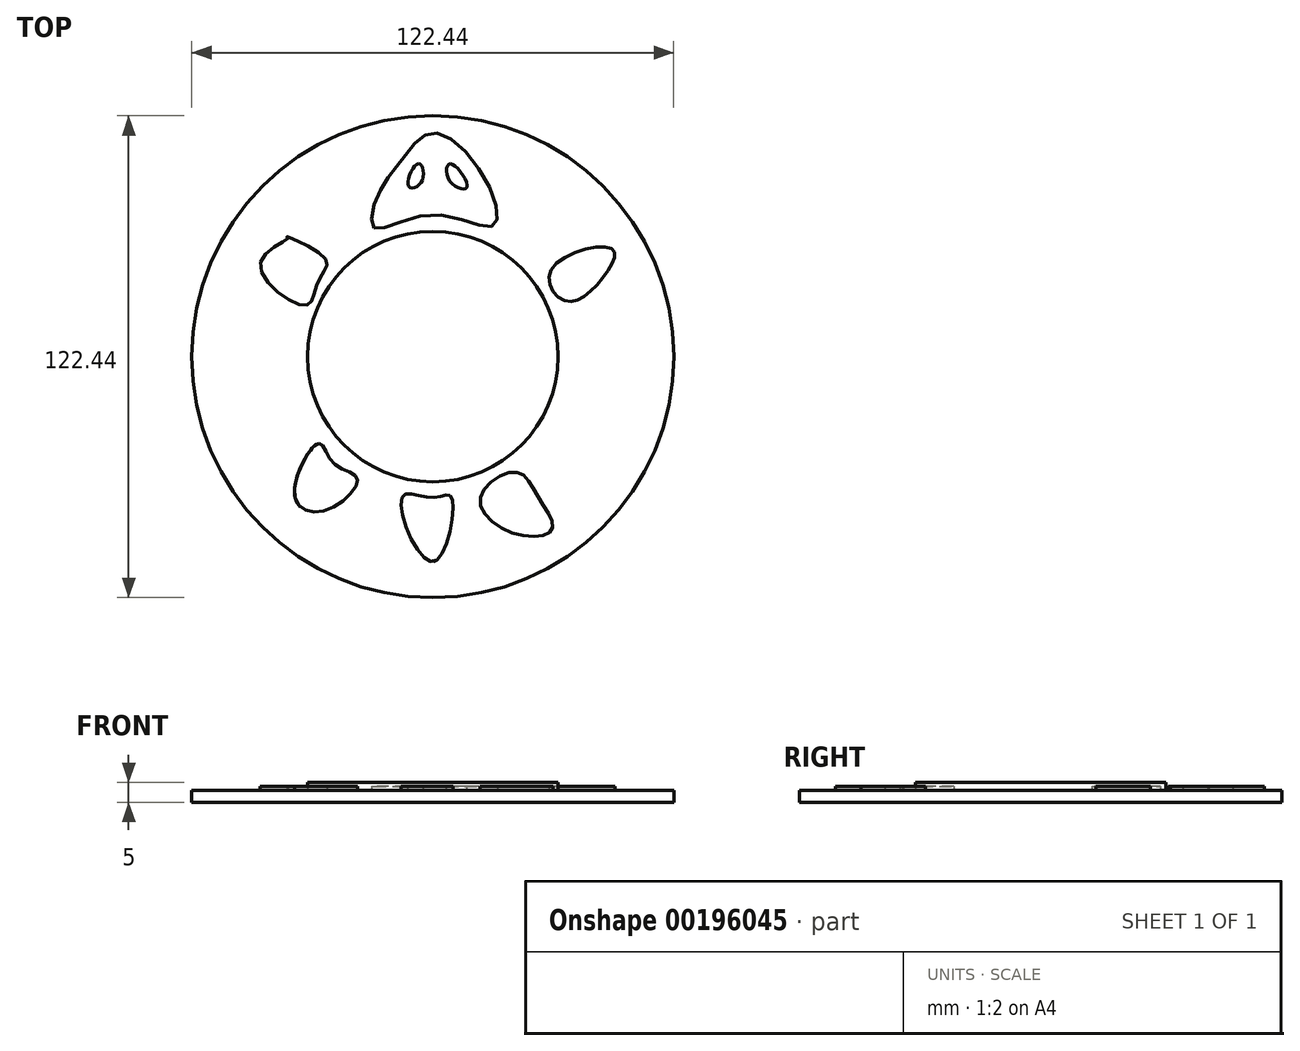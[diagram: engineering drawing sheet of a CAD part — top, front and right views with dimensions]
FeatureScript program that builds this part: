
annotation { "Feature Type Name" : "Feature", "Feature Type Description" : "" }
export const myFeature = defineFeature(function(context is Context, id is Id, definition is map)
    precondition{}
    {
        {
            var Q0;
            Q0=qCreatedBy(makeId("Top.planeOp"),FACE);
            var sketch = newSketch(context, id + "F0", { "sketchPlane" : qUnion([Q0])});
            skCircle(sketch, "E0", {"center": v(0, 0) * mm, "radius": 61.22 * mm});
            skSolve(sketch);
        }
        {
            var Q0;
            Q0 = qSketchRegion(id + "F0", true);
            extrude(context, id + "F1", {"entities" : qUnion([Q0]), "depth" : 3 * mm});
        }
        {
            var Q0;
            Q0=makeQuery(id+"F1.opExtrude","CAP_FACE",FACE,{"disambiguationData":[OSD([sQuery(id+"F0.wireOp",EDGE,"E0")])],"isStart":false});
            var sketch = newSketch(context, id + "F2", { "sketchPlane" : qUnion([Q0])});
            skCircle(sketch, "E1", {"center": v(0, 0) * mm, "radius": 31.81 * mm});
            skSolve(sketch);
        }
        {
            var Q0;
            Q0=makeQuery(id+"F2.imprint","IMPRINT",FACE,{"disambiguationData":[TD([[makeQuery(id+"F2.imprint","IMPRINT",EDGE,{"derivedFrom":sQuery(id+"F2.wireOp",EDGE,"E1")}),1.0]])]});
            extrude(context, id + "F3", {"entities" : qUnion([Q0]), "operationType" : NewBodyOperationType.ADD, "depth" : 2 * mm});
        }
        {
            var Q0;
            Q0=makeQuery(id+"F1.opExtrude","CAP_FACE",FACE,{"disambiguationData":[OSD([sQuery(id+"F0.wireOp",EDGE,"E0")])],"isStart":false});
            var sketch = newSketch(context, id + "F4", { "sketchPlane" : qUnion([Q0])});
            skFitSpline(sketch, "E2", {"points": [v(-14.88, 32.7) * mm, v(0, 36.08) * mm, v(15.44, 33.27) * mm, v(13.2, 45.34) * mm, v(0, 56.85) * mm, v(-7.3, 50.68) * mm, v(-13.76, 41.41) * mm, v(-14.88, 32.7) * mm]});
            skSolve(sketch);
        }
        {
            var Q0;
            Q0=makeQuery(id+"F4.imprint","IMPRINT",FACE,{"disambiguationData":[TD([[makeQuery(id+"F4.imprint","IMPRINT",EDGE,{"derivedFrom":sQuery(id+"F4.wireOp",EDGE,"E2")}),1.0]])]});
            extrude(context, id + "F5", {"entities" : qUnion([Q0]), "operationType" : NewBodyOperationType.ADD, "depth" : 1 * mm});
        }
        {
            var Q0;
            Q0=makeQuery(id+"F1.opExtrude","CAP_FACE",FACE,{"disambiguationData":[OSD([sQuery(id+"F0.wireOp",EDGE,"E0")])],"isStart":false});
            var sketch = newSketch(context, id + "F6", { "sketchPlane" : qUnion([Q0])});
            skFitSpline(sketch, "E3", {"points": [v(-27.23, 24.85) * mm, v(-37.06, 30.46) * mm, v(-36.78, 30.18) * mm, v(-43.8, 23.72) * mm, v(-32.29, 13.05) * mm, v(-29.2, 18.95) * mm, v(-27.23, 24.85) * mm]});
            skFitSpline(sketch, "E4", {"points": [v(-28.92, -22.04) * mm, v(-25.27, -27.1) * mm, v(-19.1, -31.02) * mm, v(-27.51, -39.16) * mm, v(-35.1, -35.23) * mm, v(-28.92, -22.04) * mm]});
            skFitSpline(sketch, "E5", {"points": [v(12.07, -35.8) * mm, v(21.06, -29.34) * mm, v(26.67, -35.51) * mm, v(30.32, -43.94) * mm, v(20.21, -44.78) * mm, v(12.07, -35.8) * mm]});
            skFitSpline(sketch, "E6", {"points": [v(30.04, 22.04) * mm, v(33.69, 14.18) * mm, v(43.24, 20.07) * mm, v(45.48, 27.37) * mm, v(30.04, 22.04) * mm]});
            skFitSpline(sketch, "E7", {"points": [v(-7.86, -35.8) * mm, v(0, -52.08) * mm, v(4.77, -35.8) * mm, v(0, -35.8) * mm, v(-7.86, -35.8) * mm]});
            skSolve(sketch);
        }
        {
            var Q0;
            Q0=makeQuery(id+"F6.imprint","IMPRINT",FACE,{"disambiguationData":[TD([[makeQuery(id+"F6.imprint","IMPRINT",EDGE,{"derivedFrom":sQuery(id+"F6.wireOp",EDGE,"E3")}),1.0]])]});
            var Q1;
            Q1=makeQuery(id+"F6.imprint","IMPRINT",FACE,{"disambiguationData":[TD([[makeQuery(id+"F6.imprint","IMPRINT",EDGE,{"derivedFrom":sQuery(id+"F6.wireOp",EDGE,"E4")}),-1.0]])]});
            var Q2;
            Q2=makeQuery(id+"F6.imprint","IMPRINT",FACE,{"disambiguationData":[TD([[makeQuery(id+"F6.imprint","IMPRINT",EDGE,{"derivedFrom":sQuery(id+"F6.wireOp",EDGE,"E7")}),1.0]])]});
            var Q3;
            Q3=makeQuery(id+"F6.imprint","IMPRINT",FACE,{"disambiguationData":[TD([[makeQuery(id+"F6.imprint","IMPRINT",EDGE,{"derivedFrom":sQuery(id+"F6.wireOp",EDGE,"E5")}),-1.0]])]});
            var Q4;
            Q4=makeQuery(id+"F6.imprint","IMPRINT",FACE,{"disambiguationData":[TD([[makeQuery(id+"F6.imprint","IMPRINT",EDGE,{"derivedFrom":sQuery(id+"F6.wireOp",EDGE,"E6")}),1.0]])]});
            extrude(context, id + "F7", {"entities" : qUnion([Q0, Q1, Q2, Q3, Q4]), "operationType" : NewBodyOperationType.ADD, "depth" : 1 * mm});
        }
        {
            var Q0;
            Q0=makeQuery(id+"F5.opExtrude","CAP_FACE",FACE,{"disambiguationData":[OSD([sQuery(id+"F4.wireOp",EDGE,"E2")])],"isStart":false});
            var sketch = newSketch(context, id + "F8", { "sketchPlane" : qUnion([Q0])});
            skFitSpline(sketch, "E8", {"points": [v(-3.65, 49) * mm, v(-6.18, 43.38) * mm, v(-2.8, 44.5) * mm, v(-3.65, 49) * mm]});
            skFitSpline(sketch, "E9", {"points": [v(4.5, 49) * mm, v(4.21, 44.78) * mm, v(8.7, 43.1) * mm, v(4.5, 49) * mm]});
            skSolve(sketch);
        }
        {
            var Q0;
            Q0=makeQuery(id+"F8.imprint","IMPRINT",FACE,{"disambiguationData":[TD([[makeQuery(id+"F8.imprint","IMPRINT",EDGE,{"derivedFrom":sQuery(id+"F8.wireOp",EDGE,"E8")}),1.0]])]});
            var Q1;
            Q1=makeQuery(id+"F8.imprint","IMPRINT",FACE,{"disambiguationData":[TD([[makeQuery(id+"F8.imprint","IMPRINT",EDGE,{"derivedFrom":sQuery(id+"F8.wireOp",EDGE,"E9")}),1.0]])]});
            extrude(context, id + "F9", {"entities" : qUnion([Q0, Q1]), "operationType" : NewBodyOperationType.REMOVE, "oppositeDirection" : true, "depth" : 1 * mm});
        }
    });
